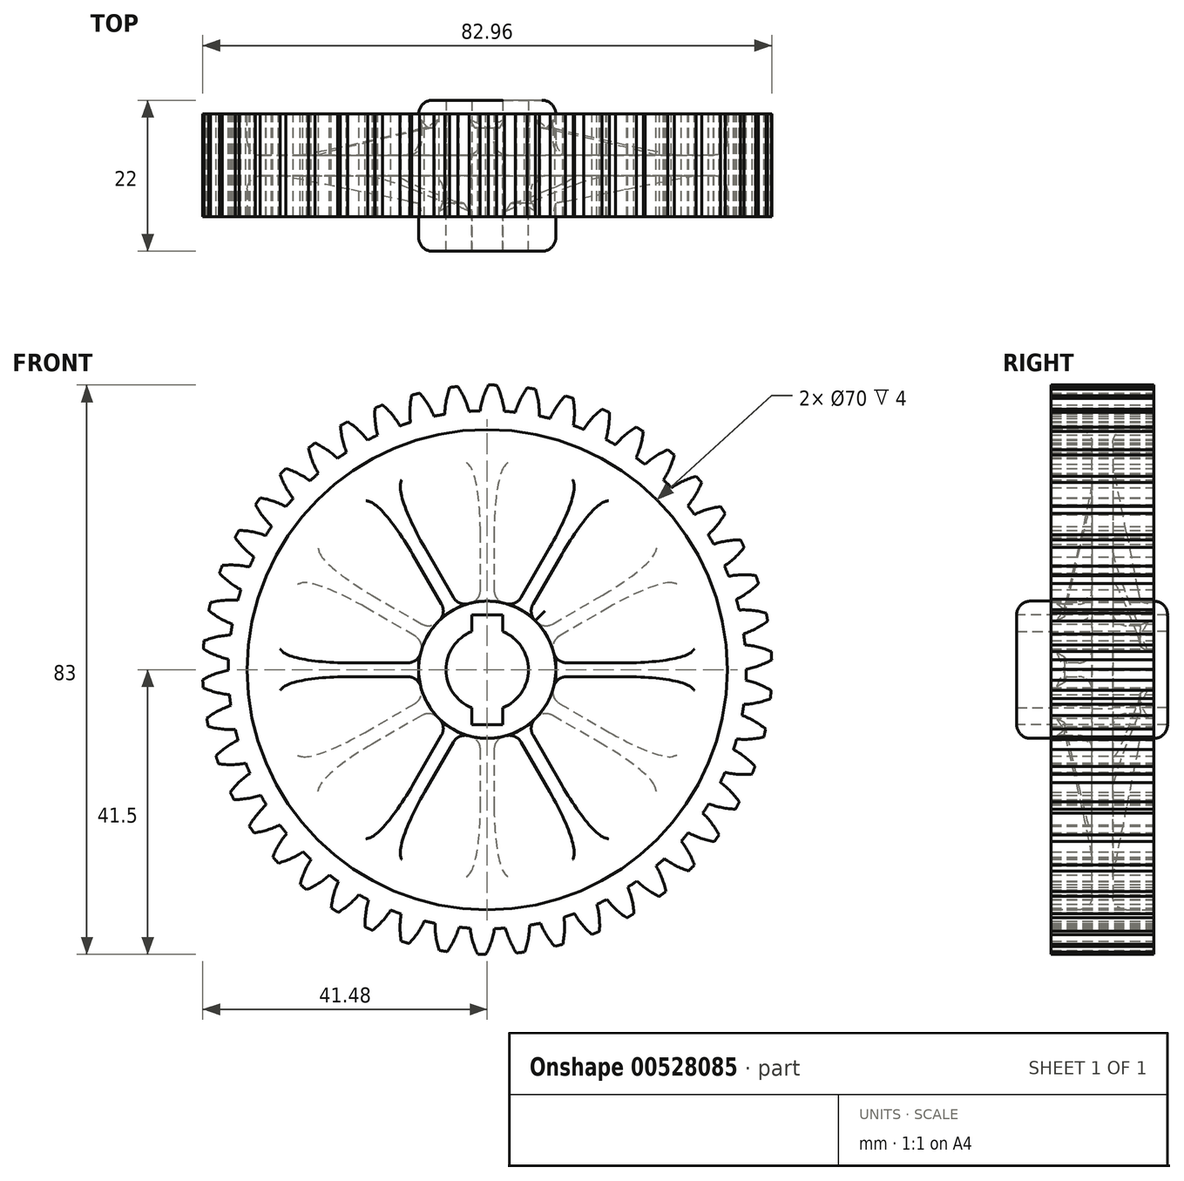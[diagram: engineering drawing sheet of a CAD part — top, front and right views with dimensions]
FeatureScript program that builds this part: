
annotation { "Feature Type Name" : "Feature", "Feature Type Description" : "" }
export const myFeature = defineFeature(function(context is Context, id is Id, definition is map)
    precondition{}
    {
        {
            var Q0;
            Q0=qCreatedBy(makeId("Front.planeOp"),FACE);
            var sketch = newSketch(context, id + "F0", { "sketchPlane" : qUnion([Q0])});
            skArc(sketch, "E0", {"start": v(1.4, 41.48) * mm, "mid": v(0.8, 41.5) * mm, "end": v(0.2, 41.5) * mm});
            skArc(sketch, "E1", {"start": v(4.12, 37.52) * mm, "mid": v(3.3, 37.6) * mm, "end": v(2.5, 37.67) * mm});
            skLineSegment(sketch, "E2", {"start": v(0, 0) * mm, "end": v(0.8, 41.5) * mm, "construction": true});
            skArc(sketch, "E3", {"start": v(0.2, 41.5) * mm, "mid": v(-0.59, 39.67) * mm, "end": v(-1.05, 37.74) * mm});
            skArc(sketch, "E4.MirrorCS", {"start": v(1.4, 41.48) * mm, "mid": v(2.1, 39.62) * mm, "end": v(2.5, 37.67) * mm});
            skArc(sketch, "E5.1.0", {"start": v(-4.27, 41.28) * mm, "mid": v(-3.31, 39.53) * mm, "end": v(-2.66, 37.66) * mm});
            skArc(sketch, "E5.1.1", {"start": v(-5.46, 41.14) * mm, "mid": v(-5.98, 39.22) * mm, "end": v(-6.18, 37.24) * mm});
            skArc(sketch, "E5.1.2", {"start": v(-4.27, 41.28) * mm, "mid": v(-4.86, 41.21) * mm, "end": v(-5.46, 41.14) * mm});
            skArc(sketch, "E5.1.3", {"start": v(-1.03, 37.74) * mm, "mid": v(-1.85, 37.7) * mm, "end": v(-2.66, 37.66) * mm});
            skArc(sketch, "E5.2.0", {"start": v(-9.85, 40.31) * mm, "mid": v(-8.67, 38.71) * mm, "end": v(-7.76, 36.94) * mm});
            skArc(sketch, "E5.2.1", {"start": v(-11.01, 40.01) * mm, "mid": v(-11.27, 38.04) * mm, "end": v(-11.2, 36.05) * mm});
            skArc(sketch, "E5.2.2", {"start": v(-9.85, 40.31) * mm, "mid": v(-10.43, 40.17) * mm, "end": v(-11.01, 40.01) * mm});
            skArc(sketch, "E5.2.3", {"start": v(-6.16, 37.24) * mm, "mid": v(-6.96, 37.1) * mm, "end": v(-7.76, 36.94) * mm});
            skArc(sketch, "E5.3.0", {"start": v(-15.25, 38.6) * mm, "mid": v(-13.86, 37.17) * mm, "end": v(-12.72, 35.54) * mm});
            skArc(sketch, "E5.3.1", {"start": v(-16.36, 38.14) * mm, "mid": v(-16.34, 36.15) * mm, "end": v(-16, 34.2) * mm});
            skArc(sketch, "E5.3.2", {"start": v(-15.25, 38.6) * mm, "mid": v(-15.8, 38.37) * mm, "end": v(-16.36, 38.14) * mm});
            skArc(sketch, "E5.3.3", {"start": v(-11.17, 36.06) * mm, "mid": v(-11.95, 35.8) * mm, "end": v(-12.72, 35.54) * mm});
            skArc(sketch, "E5.4.0", {"start": v(-20.36, 36.16) * mm, "mid": v(-18.8, 34.94) * mm, "end": v(-17.44, 33.48) * mm});
            skArc(sketch, "E5.4.1", {"start": v(-21.4, 35.56) * mm, "mid": v(-21.11, 33.59) * mm, "end": v(-20.5, 31.7) * mm});
            skArc(sketch, "E5.4.2", {"start": v(-20.36, 36.16) * mm, "mid": v(-20.88, 35.86) * mm, "end": v(-21.4, 35.56) * mm});
            skArc(sketch, "E5.4.3", {"start": v(-15.98, 34.2) * mm, "mid": v(-16.72, 33.85) * mm, "end": v(-17.44, 33.48) * mm});
            skArc(sketch, "E5.5.0", {"start": v(-25.1, 33.05) * mm, "mid": v(-23.37, 32.06) * mm, "end": v(-21.84, 30.8) * mm});
            skArc(sketch, "E5.5.1", {"start": v(-26.04, 32.31) * mm, "mid": v(-25.49, 30.4) * mm, "end": v(-24.63, 28.6) * mm});
            skArc(sketch, "E5.5.2", {"start": v(-25.1, 33.05) * mm, "mid": v(-25.57, 32.69) * mm, "end": v(-26.04, 32.31) * mm});
            skArc(sketch, "E5.5.3", {"start": v(-20.49, 31.7) * mm, "mid": v(-21.17, 31.26) * mm, "end": v(-21.84, 30.8) * mm});
            skArc(sketch, "E5.6.0", {"start": v(-29.36, 29.33) * mm, "mid": v(-27.52, 28.58) * mm, "end": v(-25.83, 27.53) * mm});
            skArc(sketch, "E5.6.1", {"start": v(-30.2, 28.47) * mm, "mid": v(-29.4, 26.65) * mm, "end": v(-28.3, 24.99) * mm});
            skArc(sketch, "E5.6.2", {"start": v(-29.36, 29.33) * mm, "mid": v(-29.78, 28.9) * mm, "end": v(-30.2, 28.47) * mm});
            skArc(sketch, "E5.6.3", {"start": v(-24.61, 28.62) * mm, "mid": v(-25.23, 28.08) * mm, "end": v(-25.83, 27.53) * mm});
            skArc(sketch, "E5.7.0", {"start": v(-33.08, 25.06) * mm, "mid": v(-31.16, 24.56) * mm, "end": v(-29.34, 23.76) * mm});
            skArc(sketch, "E5.7.1", {"start": v(-33.8, 24.09) * mm, "mid": v(-32.75, 22.4) * mm, "end": v(-31.44, 20.9) * mm});
            skArc(sketch, "E5.7.2", {"start": v(-33.08, 25.06) * mm, "mid": v(-33.44, 24.58) * mm, "end": v(-33.8, 24.09) * mm});
            skArc(sketch, "E5.7.3", {"start": v(-28.28, 25) * mm, "mid": v(-28.82, 24.39) * mm, "end": v(-29.34, 23.76) * mm});
            skArc(sketch, "E5.8.0", {"start": v(-36.19, 20.32) * mm, "mid": v(-34.2, 20.1) * mm, "end": v(-32.3, 19.54) * mm});
            skArc(sketch, "E5.8.1", {"start": v(-36.76, 19.26) * mm, "mid": v(-35.5, 17.73) * mm, "end": v(-33.99, 16.43) * mm});
            skArc(sketch, "E5.8.2", {"start": v(-36.19, 20.32) * mm, "mid": v(-36.48, 19.8) * mm, "end": v(-36.76, 19.26) * mm});
            skArc(sketch, "E5.8.3", {"start": v(-31.42, 20.92) * mm, "mid": v(-31.87, 20.24) * mm, "end": v(-32.3, 19.54) * mm});
            skArc(sketch, "E5.9.0", {"start": v(-38.62, 15.2) * mm, "mid": v(-36.63, 15.25) * mm, "end": v(-34.66, 14.96) * mm});
            skArc(sketch, "E5.9.1", {"start": v(-39.04, 14.08) * mm, "mid": v(-37.57, 12.73) * mm, "end": v(-35.9, 11.65) * mm});
            skArc(sketch, "E5.9.2", {"start": v(-38.62, 15.2) * mm, "mid": v(-38.83, 14.64) * mm, "end": v(-39.04, 14.08) * mm});
            skArc(sketch, "E5.9.3", {"start": v(-33.98, 16.45) * mm, "mid": v(-34.33, 15.7) * mm, "end": v(-34.66, 14.96) * mm});
            skArc(sketch, "E5.10.0", {"start": v(-40.33, 9.8) * mm, "mid": v(-38.36, 10.12) * mm, "end": v(-36.37, 10.1) * mm});
            skArc(sketch, "E5.10.1", {"start": v(-40.6, 8.63) * mm, "mid": v(-38.96, 7.5) * mm, "end": v(-37.16, 6.65) * mm});
            skArc(sketch, "E5.10.2", {"start": v(-40.33, 9.8) * mm, "mid": v(-40.46, 9.22) * mm, "end": v(-40.6, 8.63) * mm});
            skArc(sketch, "E5.10.3", {"start": v(-35.9, 11.67) * mm, "mid": v(-36.15, 10.89) * mm, "end": v(-36.37, 10.1) * mm});
            skArc(sketch, "E5.11.0", {"start": v(-41.28, 4.22) * mm, "mid": v(-39.38, 4.8) * mm, "end": v(-37.4, 5.06) * mm});
            skArc(sketch, "E5.11.1", {"start": v(-41.39, 3.02) * mm, "mid": v(-39.62, 2.12) * mm, "end": v(-37.72, 1.53) * mm});
            skArc(sketch, "E5.11.2", {"start": v(-41.28, 4.22) * mm, "mid": v(-41.34, 3.62) * mm, "end": v(-41.39, 3.02) * mm});
            skArc(sketch, "E5.11.3", {"start": v(-37.16, 6.67) * mm, "mid": v(-37.3, 5.86) * mm, "end": v(-37.4, 5.06) * mm});
            skArc(sketch, "E5.12.0", {"start": v(-41.48, -1.44) * mm, "mid": v(-39.67, -0.6) * mm, "end": v(-37.75, -0.08) * mm});
            skArc(sketch, "E5.12.1", {"start": v(-41.42, -2.64) * mm, "mid": v(-39.54, -3.3) * mm, "end": v(-37.58, -3.62) * mm});
            skArc(sketch, "E5.12.2", {"start": v(-41.48, -1.44) * mm, "mid": v(-41.45, -2.04) * mm, "end": v(-41.42, -2.64) * mm});
            skArc(sketch, "E5.12.3", {"start": v(-37.72, 1.55) * mm, "mid": v(-37.74, 0.73) * mm, "end": v(-37.75, -0.08) * mm});
            skArc(sketch, "E5.13.0", {"start": v(-40.9, -7.07) * mm, "mid": v(-39.22, -6) * mm, "end": v(-37.39, -5.22) * mm});
            skArc(sketch, "E5.13.1", {"start": v(-40.67, -8.26) * mm, "mid": v(-38.72, -8.64) * mm, "end": v(-36.73, -8.7) * mm});
            skArc(sketch, "E5.13.2", {"start": v(-40.9, -7.07) * mm, "mid": v(-40.79, -7.67) * mm, "end": v(-40.67, -8.26) * mm});
            skArc(sketch, "E5.13.3", {"start": v(-37.58, -3.6) * mm, "mid": v(-37.5, -4.42) * mm, "end": v(-37.39, -5.22) * mm});
            skArc(sketch, "E5.14.0", {"start": v(-39.55, -12.58) * mm, "mid": v(-38.03, -11.29) * mm, "end": v(-36.33, -10.27) * mm});
            skArc(sketch, "E5.14.1", {"start": v(-39.17, -13.72) * mm, "mid": v(-37.18, -13.84) * mm, "end": v(-35.2, -13.63) * mm});
            skArc(sketch, "E5.14.2", {"start": v(-39.55, -12.58) * mm, "mid": v(-39.36, -13.15) * mm, "end": v(-39.17, -13.72) * mm});
            skArc(sketch, "E5.14.3", {"start": v(-36.74, -8.69) * mm, "mid": v(-36.54, -9.48) * mm, "end": v(-36.33, -10.27) * mm});
            skArc(sketch, "E5.15.0", {"start": v(-37.47, -17.84) * mm, "mid": v(-36.14, -16.36) * mm, "end": v(-34.6, -15.12) * mm});
            skArc(sketch, "E5.15.1", {"start": v(-36.93, -18.92) * mm, "mid": v(-34.95, -18.77) * mm, "end": v(-33.02, -18.3) * mm});
            skArc(sketch, "E5.15.2", {"start": v(-37.47, -17.84) * mm, "mid": v(-37.2, -18.39) * mm, "end": v(-36.93, -18.92) * mm});
            skArc(sketch, "E5.15.3", {"start": v(-35.21, -13.6) * mm, "mid": v(-34.9, -14.37) * mm, "end": v(-34.6, -15.12) * mm});
            skArc(sketch, "E5.16.0", {"start": v(-34.69, -22.78) * mm, "mid": v(-33.58, -21.13) * mm, "end": v(-32.21, -19.69) * mm});
            skArc(sketch, "E5.16.1", {"start": v(-34.01, -23.78) * mm, "mid": v(-32.07, -23.35) * mm, "end": v(-30.22, -22.62) * mm});
            skArc(sketch, "E5.16.2", {"start": v(-34.69, -22.78) * mm, "mid": v(-34.36, -23.28) * mm, "end": v(-34.01, -23.78) * mm});
            skArc(sketch, "E5.16.3", {"start": v(-33.03, -18.28) * mm, "mid": v(-32.63, -18.99) * mm, "end": v(-32.21, -19.69) * mm});
            skArc(sketch, "E5.17.0", {"start": v(-31.26, -27.3) * mm, "mid": v(-30.39, -25.5) * mm, "end": v(-29.23, -23.89) * mm});
            skArc(sketch, "E5.17.1", {"start": v(-30.46, -28.19) * mm, "mid": v(-28.6, -27.5) * mm, "end": v(-26.86, -26.52) * mm});
            skArc(sketch, "E5.17.2", {"start": v(-31.26, -27.3) * mm, "mid": v(-30.87, -27.74) * mm, "end": v(-30.46, -28.19) * mm});
            skArc(sketch, "E5.17.3", {"start": v(-30.23, -22.6) * mm, "mid": v(-29.74, -23.25) * mm, "end": v(-29.23, -23.89) * mm});
            skArc(sketch, "E5.18.0", {"start": v(-27.26, -31.3) * mm, "mid": v(-26.63, -29.4) * mm, "end": v(-25.7, -27.65) * mm});
            skArc(sketch, "E5.18.1", {"start": v(-26.34, -32.07) * mm, "mid": v(-24.58, -31.14) * mm, "end": v(-23, -29.94) * mm});
            skArc(sketch, "E5.18.2", {"start": v(-27.26, -31.3) * mm, "mid": v(-26.8, -31.69) * mm, "end": v(-26.34, -32.07) * mm});
            skArc(sketch, "E5.18.3", {"start": v(-26.87, -26.51) * mm, "mid": v(-26.3, -27.08) * mm, "end": v(-25.7, -27.65) * mm});
            skArc(sketch, "E5.19.0", {"start": v(-22.74, -34.71) * mm, "mid": v(-22.38, -32.76) * mm, "end": v(-21.7, -30.89) * mm});
            skArc(sketch, "E5.19.1", {"start": v(-21.73, -35.36) * mm, "mid": v(-20.11, -34.2) * mm, "end": v(-18.7, -32.79) * mm});
            skArc(sketch, "E5.19.2", {"start": v(-22.74, -34.71) * mm, "mid": v(-22.24, -35.04) * mm, "end": v(-21.73, -35.36) * mm});
            skArc(sketch, "E5.19.3", {"start": v(-23.01, -29.92) * mm, "mid": v(-22.36, -30.41) * mm, "end": v(-21.7, -30.89) * mm});
            skArc(sketch, "E5.20.0", {"start": v(-17.8, -37.49) * mm, "mid": v(-17.7, -35.5) * mm, "end": v(-17.3, -33.56) * mm});
            skArc(sketch, "E5.20.1", {"start": v(-16.7, -37.99) * mm, "mid": v(-15.27, -36.62) * mm, "end": v(-14.07, -35.03) * mm});
            skArc(sketch, "E5.20.2", {"start": v(-17.8, -37.49) * mm, "mid": v(-17.26, -37.74) * mm, "end": v(-16.7, -37.99) * mm});
            skArc(sketch, "E5.20.3", {"start": v(-18.73, -32.78) * mm, "mid": v(-18.01, -33.18) * mm, "end": v(-17.3, -33.56) * mm});
            skArc(sketch, "E5.21.0", {"start": v(-12.53, -39.56) * mm, "mid": v(-12.71, -37.58) * mm, "end": v(-12.56, -35.6) * mm});
            skArc(sketch, "E5.21.1", {"start": v(-11.38, -39.9) * mm, "mid": v(-10.14, -38.36) * mm, "end": v(-9.17, -36.62) * mm});
            skArc(sketch, "E5.21.2", {"start": v(-12.53, -39.56) * mm, "mid": v(-11.96, -39.74) * mm, "end": v(-11.38, -39.9) * mm});
            skArc(sketch, "E5.21.3", {"start": v(-14.09, -35.02) * mm, "mid": v(-13.33, -35.32) * mm, "end": v(-12.56, -35.6) * mm});
            skArc(sketch, "E5.22.0", {"start": v(-7.03, -40.9) * mm, "mid": v(-7.47, -38.96) * mm, "end": v(-7.6, -36.98) * mm});
            skArc(sketch, "E5.22.1", {"start": v(-5.84, -41.09) * mm, "mid": v(-4.82, -39.38) * mm, "end": v(-4.1, -37.53) * mm});
            skArc(sketch, "E5.22.2", {"start": v(-7.03, -40.9) * mm, "mid": v(-6.44, -41) * mm, "end": v(-5.84, -41.09) * mm});
            skArc(sketch, "E5.22.3", {"start": v(-9.19, -36.61) * mm, "mid": v(-8.4, -36.8) * mm, "end": v(-7.6, -36.98) * mm});
            skArc(sketch, "E5.23.0", {"start": v(-1.4, -41.48) * mm, "mid": v(-2.1, -39.62) * mm, "end": v(-2.5, -37.67) * mm});
            skArc(sketch, "E5.23.1", {"start": v(-0.2, -41.5) * mm, "mid": v(0.59, -39.67) * mm, "end": v(1.05, -37.74) * mm});
            skArc(sketch, "E5.23.2", {"start": v(-1.4, -41.48) * mm, "mid": v(-0.8, -41.5) * mm, "end": v(-0.2, -41.5) * mm});
            skArc(sketch, "E5.23.3", {"start": v(-4.12, -37.52) * mm, "mid": v(-3.3, -37.6) * mm, "end": v(-2.5, -37.67) * mm});
            skArc(sketch, "E5.24.0", {"start": v(4.27, -41.28) * mm, "mid": v(3.31, -39.53) * mm, "end": v(2.66, -37.66) * mm});
            skArc(sketch, "E5.24.1", {"start": v(5.46, -41.14) * mm, "mid": v(5.98, -39.22) * mm, "end": v(6.18, -37.24) * mm});
            skArc(sketch, "E5.24.2", {"start": v(4.27, -41.28) * mm, "mid": v(4.86, -41.21) * mm, "end": v(5.46, -41.14) * mm});
            skArc(sketch, "E5.24.3", {"start": v(1.03, -37.74) * mm, "mid": v(1.85, -37.7) * mm, "end": v(2.66, -37.66) * mm});
            skArc(sketch, "E5.25.0", {"start": v(9.85, -40.31) * mm, "mid": v(8.67, -38.71) * mm, "end": v(7.76, -36.94) * mm});
            skArc(sketch, "E5.25.1", {"start": v(11.01, -40.01) * mm, "mid": v(11.27, -38.04) * mm, "end": v(11.2, -36.05) * mm});
            skArc(sketch, "E5.25.2", {"start": v(9.85, -40.31) * mm, "mid": v(10.43, -40.17) * mm, "end": v(11.01, -40.01) * mm});
            skArc(sketch, "E5.25.3", {"start": v(6.16, -37.24) * mm, "mid": v(6.96, -37.1) * mm, "end": v(7.76, -36.94) * mm});
            skArc(sketch, "E5.26.0", {"start": v(15.25, -38.6) * mm, "mid": v(13.86, -37.17) * mm, "end": v(12.72, -35.54) * mm});
            skArc(sketch, "E5.26.1", {"start": v(16.36, -38.14) * mm, "mid": v(16.34, -36.15) * mm, "end": v(16, -34.2) * mm});
            skArc(sketch, "E5.26.2", {"start": v(15.25, -38.6) * mm, "mid": v(15.8, -38.37) * mm, "end": v(16.36, -38.14) * mm});
            skArc(sketch, "E5.26.3", {"start": v(11.17, -36.06) * mm, "mid": v(11.95, -35.8) * mm, "end": v(12.72, -35.54) * mm});
            skArc(sketch, "E5.27.0", {"start": v(20.36, -36.16) * mm, "mid": v(18.8, -34.94) * mm, "end": v(17.44, -33.48) * mm});
            skArc(sketch, "E5.27.1", {"start": v(21.4, -35.56) * mm, "mid": v(21.11, -33.59) * mm, "end": v(20.5, -31.7) * mm});
            skArc(sketch, "E5.27.2", {"start": v(20.36, -36.16) * mm, "mid": v(20.88, -35.86) * mm, "end": v(21.4, -35.56) * mm});
            skArc(sketch, "E5.27.3", {"start": v(15.98, -34.2) * mm, "mid": v(16.72, -33.85) * mm, "end": v(17.44, -33.48) * mm});
            skArc(sketch, "E5.28.0", {"start": v(25.1, -33.05) * mm, "mid": v(23.37, -32.06) * mm, "end": v(21.84, -30.8) * mm});
            skArc(sketch, "E5.28.1", {"start": v(26.04, -32.31) * mm, "mid": v(25.49, -30.4) * mm, "end": v(24.63, -28.6) * mm});
            skArc(sketch, "E5.28.2", {"start": v(25.1, -33.05) * mm, "mid": v(25.57, -32.69) * mm, "end": v(26.04, -32.31) * mm});
            skArc(sketch, "E5.28.3", {"start": v(20.49, -31.7) * mm, "mid": v(21.17, -31.26) * mm, "end": v(21.84, -30.8) * mm});
            skArc(sketch, "E5.29.0", {"start": v(29.36, -29.33) * mm, "mid": v(27.52, -28.58) * mm, "end": v(25.83, -27.53) * mm});
            skArc(sketch, "E5.29.1", {"start": v(30.2, -28.47) * mm, "mid": v(29.4, -26.65) * mm, "end": v(28.3, -24.99) * mm});
            skArc(sketch, "E5.29.2", {"start": v(29.36, -29.33) * mm, "mid": v(29.78, -28.9) * mm, "end": v(30.2, -28.47) * mm});
            skArc(sketch, "E5.29.3", {"start": v(24.61, -28.62) * mm, "mid": v(25.23, -28.08) * mm, "end": v(25.83, -27.53) * mm});
            skArc(sketch, "E5.30.0", {"start": v(33.08, -25.06) * mm, "mid": v(31.16, -24.56) * mm, "end": v(29.34, -23.76) * mm});
            skArc(sketch, "E5.30.1", {"start": v(33.8, -24.09) * mm, "mid": v(32.75, -22.4) * mm, "end": v(31.44, -20.9) * mm});
            skArc(sketch, "E5.30.2", {"start": v(33.08, -25.06) * mm, "mid": v(33.44, -24.58) * mm, "end": v(33.8, -24.09) * mm});
            skArc(sketch, "E5.30.3", {"start": v(28.28, -25) * mm, "mid": v(28.82, -24.39) * mm, "end": v(29.34, -23.76) * mm});
            skArc(sketch, "E5.31.0", {"start": v(36.19, -20.32) * mm, "mid": v(34.2, -20.1) * mm, "end": v(32.3, -19.54) * mm});
            skArc(sketch, "E5.31.1", {"start": v(36.76, -19.26) * mm, "mid": v(35.5, -17.73) * mm, "end": v(33.99, -16.43) * mm});
            skArc(sketch, "E5.31.2", {"start": v(36.19, -20.32) * mm, "mid": v(36.48, -19.8) * mm, "end": v(36.76, -19.26) * mm});
            skArc(sketch, "E5.31.3", {"start": v(31.42, -20.92) * mm, "mid": v(31.87, -20.24) * mm, "end": v(32.3, -19.54) * mm});
            skArc(sketch, "E5.32.0", {"start": v(38.62, -15.2) * mm, "mid": v(36.63, -15.25) * mm, "end": v(34.66, -14.96) * mm});
            skArc(sketch, "E5.32.1", {"start": v(39.04, -14.08) * mm, "mid": v(37.57, -12.73) * mm, "end": v(35.9, -11.65) * mm});
            skArc(sketch, "E5.32.2", {"start": v(38.62, -15.2) * mm, "mid": v(38.83, -14.64) * mm, "end": v(39.04, -14.08) * mm});
            skArc(sketch, "E5.32.3", {"start": v(33.98, -16.45) * mm, "mid": v(34.33, -15.7) * mm, "end": v(34.66, -14.96) * mm});
            skArc(sketch, "E5.33.0", {"start": v(40.33, -9.8) * mm, "mid": v(38.36, -10.12) * mm, "end": v(36.37, -10.1) * mm});
            skArc(sketch, "E5.33.1", {"start": v(40.6, -8.63) * mm, "mid": v(38.96, -7.5) * mm, "end": v(37.16, -6.65) * mm});
            skArc(sketch, "E5.33.2", {"start": v(40.33, -9.8) * mm, "mid": v(40.46, -9.22) * mm, "end": v(40.6, -8.63) * mm});
            skArc(sketch, "E5.33.3", {"start": v(35.9, -11.67) * mm, "mid": v(36.15, -10.89) * mm, "end": v(36.37, -10.1) * mm});
            skArc(sketch, "E5.34.0", {"start": v(41.28, -4.22) * mm, "mid": v(39.38, -4.8) * mm, "end": v(37.4, -5.06) * mm});
            skArc(sketch, "E5.34.1", {"start": v(41.39, -3.02) * mm, "mid": v(39.62, -2.12) * mm, "end": v(37.72, -1.53) * mm});
            skArc(sketch, "E5.34.2", {"start": v(41.28, -4.22) * mm, "mid": v(41.34, -3.62) * mm, "end": v(41.39, -3.02) * mm});
            skArc(sketch, "E5.34.3", {"start": v(37.16, -6.67) * mm, "mid": v(37.3, -5.86) * mm, "end": v(37.4, -5.06) * mm});
            skArc(sketch, "E5.35.0", {"start": v(41.48, 1.44) * mm, "mid": v(39.67, 0.6) * mm, "end": v(37.75, 0.08) * mm});
            skArc(sketch, "E5.35.1", {"start": v(41.42, 2.64) * mm, "mid": v(39.54, 3.3) * mm, "end": v(37.58, 3.62) * mm});
            skArc(sketch, "E5.35.2", {"start": v(41.48, 1.44) * mm, "mid": v(41.45, 2.04) * mm, "end": v(41.42, 2.64) * mm});
            skArc(sketch, "E5.35.3", {"start": v(37.72, -1.55) * mm, "mid": v(37.74, -0.73) * mm, "end": v(37.75, 0.08) * mm});
            skArc(sketch, "E5.36.0", {"start": v(40.9, 7.07) * mm, "mid": v(39.22, 6) * mm, "end": v(37.39, 5.22) * mm});
            skArc(sketch, "E5.36.1", {"start": v(40.67, 8.26) * mm, "mid": v(38.72, 8.64) * mm, "end": v(36.73, 8.7) * mm});
            skArc(sketch, "E5.36.2", {"start": v(40.9, 7.07) * mm, "mid": v(40.79, 7.67) * mm, "end": v(40.67, 8.26) * mm});
            skArc(sketch, "E5.36.3", {"start": v(37.58, 3.6) * mm, "mid": v(37.5, 4.42) * mm, "end": v(37.39, 5.22) * mm});
            skArc(sketch, "E5.37.0", {"start": v(39.55, 12.58) * mm, "mid": v(38.03, 11.29) * mm, "end": v(36.33, 10.27) * mm});
            skArc(sketch, "E5.37.1", {"start": v(39.17, 13.72) * mm, "mid": v(37.18, 13.84) * mm, "end": v(35.2, 13.63) * mm});
            skArc(sketch, "E5.37.2", {"start": v(39.55, 12.58) * mm, "mid": v(39.36, 13.15) * mm, "end": v(39.17, 13.72) * mm});
            skArc(sketch, "E5.37.3", {"start": v(36.74, 8.69) * mm, "mid": v(36.54, 9.48) * mm, "end": v(36.33, 10.27) * mm});
            skArc(sketch, "E5.38.0", {"start": v(37.47, 17.84) * mm, "mid": v(36.14, 16.36) * mm, "end": v(34.6, 15.12) * mm});
            skArc(sketch, "E5.38.1", {"start": v(36.93, 18.92) * mm, "mid": v(34.95, 18.77) * mm, "end": v(33.02, 18.3) * mm});
            skArc(sketch, "E5.38.2", {"start": v(37.47, 17.84) * mm, "mid": v(37.2, 18.39) * mm, "end": v(36.93, 18.92) * mm});
            skArc(sketch, "E5.38.3", {"start": v(35.21, 13.6) * mm, "mid": v(34.9, 14.37) * mm, "end": v(34.6, 15.12) * mm});
            skArc(sketch, "E5.39.0", {"start": v(34.69, 22.78) * mm, "mid": v(33.58, 21.13) * mm, "end": v(32.21, 19.69) * mm});
            skArc(sketch, "E5.39.1", {"start": v(34.01, 23.78) * mm, "mid": v(32.07, 23.35) * mm, "end": v(30.22, 22.62) * mm});
            skArc(sketch, "E5.39.2", {"start": v(34.69, 22.78) * mm, "mid": v(34.36, 23.28) * mm, "end": v(34.01, 23.78) * mm});
            skArc(sketch, "E5.39.3", {"start": v(33.03, 18.28) * mm, "mid": v(32.63, 18.99) * mm, "end": v(32.21, 19.69) * mm});
            skArc(sketch, "E5.40.0", {"start": v(31.26, 27.3) * mm, "mid": v(30.39, 25.5) * mm, "end": v(29.23, 23.89) * mm});
            skArc(sketch, "E5.40.1", {"start": v(30.46, 28.19) * mm, "mid": v(28.6, 27.5) * mm, "end": v(26.86, 26.52) * mm});
            skArc(sketch, "E5.40.2", {"start": v(31.26, 27.3) * mm, "mid": v(30.87, 27.74) * mm, "end": v(30.46, 28.19) * mm});
            skArc(sketch, "E5.40.3", {"start": v(30.23, 22.6) * mm, "mid": v(29.74, 23.25) * mm, "end": v(29.23, 23.89) * mm});
            skArc(sketch, "E5.41.0", {"start": v(27.26, 31.3) * mm, "mid": v(26.63, 29.4) * mm, "end": v(25.7, 27.65) * mm});
            skArc(sketch, "E5.41.1", {"start": v(26.34, 32.07) * mm, "mid": v(24.58, 31.14) * mm, "end": v(23, 29.94) * mm});
            skArc(sketch, "E5.41.2", {"start": v(27.26, 31.3) * mm, "mid": v(26.8, 31.69) * mm, "end": v(26.34, 32.07) * mm});
            skArc(sketch, "E5.41.3", {"start": v(26.87, 26.51) * mm, "mid": v(26.3, 27.08) * mm, "end": v(25.7, 27.65) * mm});
            skArc(sketch, "E5.42.0", {"start": v(22.74, 34.71) * mm, "mid": v(22.38, 32.76) * mm, "end": v(21.7, 30.89) * mm});
            skArc(sketch, "E5.42.1", {"start": v(21.73, 35.36) * mm, "mid": v(20.11, 34.2) * mm, "end": v(18.7, 32.79) * mm});
            skArc(sketch, "E5.42.2", {"start": v(22.74, 34.71) * mm, "mid": v(22.24, 35.04) * mm, "end": v(21.73, 35.36) * mm});
            skArc(sketch, "E5.42.3", {"start": v(23.01, 29.92) * mm, "mid": v(22.36, 30.41) * mm, "end": v(21.7, 30.89) * mm});
            skArc(sketch, "E5.43.0", {"start": v(17.8, 37.49) * mm, "mid": v(17.7, 35.5) * mm, "end": v(17.3, 33.56) * mm});
            skArc(sketch, "E5.43.1", {"start": v(16.7, 37.99) * mm, "mid": v(15.27, 36.62) * mm, "end": v(14.07, 35.03) * mm});
            skArc(sketch, "E5.43.2", {"start": v(17.8, 37.49) * mm, "mid": v(17.26, 37.74) * mm, "end": v(16.7, 37.99) * mm});
            skArc(sketch, "E5.43.3", {"start": v(18.73, 32.78) * mm, "mid": v(18.01, 33.18) * mm, "end": v(17.3, 33.56) * mm});
            skArc(sketch, "E5.44.0", {"start": v(12.53, 39.56) * mm, "mid": v(12.71, 37.58) * mm, "end": v(12.56, 35.6) * mm});
            skArc(sketch, "E5.44.1", {"start": v(11.38, 39.9) * mm, "mid": v(10.14, 38.36) * mm, "end": v(9.17, 36.62) * mm});
            skArc(sketch, "E5.44.2", {"start": v(12.53, 39.56) * mm, "mid": v(11.96, 39.74) * mm, "end": v(11.38, 39.9) * mm});
            skArc(sketch, "E5.44.3", {"start": v(14.09, 35.02) * mm, "mid": v(13.33, 35.32) * mm, "end": v(12.56, 35.6) * mm});
            skArc(sketch, "E5.45.0", {"start": v(7.03, 40.9) * mm, "mid": v(7.47, 38.96) * mm, "end": v(7.6, 36.98) * mm});
            skArc(sketch, "E5.45.1", {"start": v(5.84, 41.09) * mm, "mid": v(4.82, 39.38) * mm, "end": v(4.1, 37.53) * mm});
            skArc(sketch, "E5.45.2", {"start": v(7.03, 40.9) * mm, "mid": v(6.44, 41) * mm, "end": v(5.84, 41.09) * mm});
            skArc(sketch, "E5.45.3", {"start": v(9.19, 36.61) * mm, "mid": v(8.4, 36.8) * mm, "end": v(7.6, 36.98) * mm});
            skCircle(sketch, "E6", {"center": v(0, 0) * mm, "radius": 6.1 * mm});
            skSolve(sketch);
        }
        {
            var Q0;
            Q0 = qSketchRegion(id + "F0", true);
            extrude(context, id + "F1", {"entities" : qUnion([Q0]), "depth" : 15 * mm, "offsetDistance" : 25 * mm});
        }
        {
            var Q0;
            Q0=makeQuery(id+"F1.opExtrude","CAP_FACE",FACE,{"disambiguationData":[OSD([sQuery(id+"F0.wireOp",EDGE,"E0"),sQuery(id+"F0.wireOp",EDGE,"E1"),sQuery(id+"F0.wireOp",EDGE,"E3"),sQuery(id+"F0.wireOp",EDGE,"E4.MirrorCS"),sQuery(id+"F0.wireOp",EDGE,"E5.1.0"),sQuery(id+"F0.wireOp",EDGE,"E5.1.1"),sQuery(id+"F0.wireOp",EDGE,"E5.1.2"),sQuery(id+"F0.wireOp",EDGE,"E5.1.3"),sQuery(id+"F0.wireOp",EDGE,"E5.2.0"),sQuery(id+"F0.wireOp",EDGE,"E5.2.1"),sQuery(id+"F0.wireOp",EDGE,"E5.2.2"),sQuery(id+"F0.wireOp",EDGE,"E5.2.3"),sQuery(id+"F0.wireOp",EDGE,"E5.3.0"),sQuery(id+"F0.wireOp",EDGE,"E5.3.1"),sQuery(id+"F0.wireOp",EDGE,"E5.3.2"),sQuery(id+"F0.wireOp",EDGE,"E5.3.3"),sQuery(id+"F0.wireOp",EDGE,"E5.4.0"),sQuery(id+"F0.wireOp",EDGE,"E5.4.1"),sQuery(id+"F0.wireOp",EDGE,"E5.4.2"),sQuery(id+"F0.wireOp",EDGE,"E5.4.3"),sQuery(id+"F0.wireOp",EDGE,"E5.5.0"),sQuery(id+"F0.wireOp",EDGE,"E5.5.1"),sQuery(id+"F0.wireOp",EDGE,"E5.5.2"),sQuery(id+"F0.wireOp",EDGE,"E5.5.3"),sQuery(id+"F0.wireOp",EDGE,"E5.6.0"),sQuery(id+"F0.wireOp",EDGE,"E5.6.1"),sQuery(id+"F0.wireOp",EDGE,"E5.6.2"),sQuery(id+"F0.wireOp",EDGE,"E5.6.3"),sQuery(id+"F0.wireOp",EDGE,"E5.7.0"),sQuery(id+"F0.wireOp",EDGE,"E5.7.1"),sQuery(id+"F0.wireOp",EDGE,"E5.7.2"),sQuery(id+"F0.wireOp",EDGE,"E5.7.3"),sQuery(id+"F0.wireOp",EDGE,"E5.8.0"),sQuery(id+"F0.wireOp",EDGE,"E5.8.1"),sQuery(id+"F0.wireOp",EDGE,"E5.8.2"),sQuery(id+"F0.wireOp",EDGE,"E5.8.3"),sQuery(id+"F0.wireOp",EDGE,"E5.9.0"),sQuery(id+"F0.wireOp",EDGE,"E5.9.1"),sQuery(id+"F0.wireOp",EDGE,"E5.9.2"),sQuery(id+"F0.wireOp",EDGE,"E5.9.3"),sQuery(id+"F0.wireOp",EDGE,"E5.10.0"),sQuery(id+"F0.wireOp",EDGE,"E5.10.1"),sQuery(id+"F0.wireOp",EDGE,"E5.10.2"),sQuery(id+"F0.wireOp",EDGE,"E5.10.3"),sQuery(id+"F0.wireOp",EDGE,"E5.11.0"),sQuery(id+"F0.wireOp",EDGE,"E5.11.1"),sQuery(id+"F0.wireOp",EDGE,"E5.11.2"),sQuery(id+"F0.wireOp",EDGE,"E5.11.3"),sQuery(id+"F0.wireOp",EDGE,"E5.12.0"),sQuery(id+"F0.wireOp",EDGE,"E5.12.1"),sQuery(id+"F0.wireOp",EDGE,"E5.12.2"),sQuery(id+"F0.wireOp",EDGE,"E5.12.3"),sQuery(id+"F0.wireOp",EDGE,"E5.13.0"),sQuery(id+"F0.wireOp",EDGE,"E5.13.1"),sQuery(id+"F0.wireOp",EDGE,"E5.13.2"),sQuery(id+"F0.wireOp",EDGE,"E5.13.3"),sQuery(id+"F0.wireOp",EDGE,"E5.14.0"),sQuery(id+"F0.wireOp",EDGE,"E5.14.1"),sQuery(id+"F0.wireOp",EDGE,"E5.14.2"),sQuery(id+"F0.wireOp",EDGE,"E5.14.3"),sQuery(id+"F0.wireOp",EDGE,"E5.15.0"),sQuery(id+"F0.wireOp",EDGE,"E5.15.1"),sQuery(id+"F0.wireOp",EDGE,"E5.15.2"),sQuery(id+"F0.wireOp",EDGE,"E5.15.3"),sQuery(id+"F0.wireOp",EDGE,"E5.16.0"),sQuery(id+"F0.wireOp",EDGE,"E5.16.1"),sQuery(id+"F0.wireOp",EDGE,"E5.16.2"),sQuery(id+"F0.wireOp",EDGE,"E5.16.3"),sQuery(id+"F0.wireOp",EDGE,"E5.17.0"),sQuery(id+"F0.wireOp",EDGE,"E5.17.1"),sQuery(id+"F0.wireOp",EDGE,"E5.17.2"),sQuery(id+"F0.wireOp",EDGE,"E5.17.3"),sQuery(id+"F0.wireOp",EDGE,"E5.18.0"),sQuery(id+"F0.wireOp",EDGE,"E5.18.1"),sQuery(id+"F0.wireOp",EDGE,"E5.18.2"),sQuery(id+"F0.wireOp",EDGE,"E5.18.3"),sQuery(id+"F0.wireOp",EDGE,"E5.19.0"),sQuery(id+"F0.wireOp",EDGE,"E5.19.1"),sQuery(id+"F0.wireOp",EDGE,"E5.19.2"),sQuery(id+"F0.wireOp",EDGE,"E5.19.3"),sQuery(id+"F0.wireOp",EDGE,"E5.20.0"),sQuery(id+"F0.wireOp",EDGE,"E5.20.1"),sQuery(id+"F0.wireOp",EDGE,"E5.20.2"),sQuery(id+"F0.wireOp",EDGE,"E5.20.3"),sQuery(id+"F0.wireOp",EDGE,"E5.21.0"),sQuery(id+"F0.wireOp",EDGE,"E5.21.1"),sQuery(id+"F0.wireOp",EDGE,"E5.21.2"),sQuery(id+"F0.wireOp",EDGE,"E5.21.3"),sQuery(id+"F0.wireOp",EDGE,"E5.22.0"),sQuery(id+"F0.wireOp",EDGE,"E5.22.1"),sQuery(id+"F0.wireOp",EDGE,"E5.22.2"),sQuery(id+"F0.wireOp",EDGE,"E5.22.3"),sQuery(id+"F0.wireOp",EDGE,"E5.23.0"),sQuery(id+"F0.wireOp",EDGE,"E5.23.1"),sQuery(id+"F0.wireOp",EDGE,"E5.23.2"),sQuery(id+"F0.wireOp",EDGE,"E5.23.3"),sQuery(id+"F0.wireOp",EDGE,"E5.24.0"),sQuery(id+"F0.wireOp",EDGE,"E5.24.1"),sQuery(id+"F0.wireOp",EDGE,"E5.24.2"),sQuery(id+"F0.wireOp",EDGE,"E5.24.3"),sQuery(id+"F0.wireOp",EDGE,"E5.25.0"),sQuery(id+"F0.wireOp",EDGE,"E5.25.1"),sQuery(id+"F0.wireOp",EDGE,"E5.25.2"),sQuery(id+"F0.wireOp",EDGE,"E5.25.3"),sQuery(id+"F0.wireOp",EDGE,"E5.26.0"),sQuery(id+"F0.wireOp",EDGE,"E5.26.1"),sQuery(id+"F0.wireOp",EDGE,"E5.26.2"),sQuery(id+"F0.wireOp",EDGE,"E5.26.3"),sQuery(id+"F0.wireOp",EDGE,"E5.27.0"),sQuery(id+"F0.wireOp",EDGE,"E5.27.1"),sQuery(id+"F0.wireOp",EDGE,"E5.27.2"),sQuery(id+"F0.wireOp",EDGE,"E5.27.3"),sQuery(id+"F0.wireOp",EDGE,"E5.28.0"),sQuery(id+"F0.wireOp",EDGE,"E5.28.1"),sQuery(id+"F0.wireOp",EDGE,"E5.28.2"),sQuery(id+"F0.wireOp",EDGE,"E5.28.3"),sQuery(id+"F0.wireOp",EDGE,"E5.29.0"),sQuery(id+"F0.wireOp",EDGE,"E5.29.1"),sQuery(id+"F0.wireOp",EDGE,"E5.29.2"),sQuery(id+"F0.wireOp",EDGE,"E5.29.3"),sQuery(id+"F0.wireOp",EDGE,"E5.30.0"),sQuery(id+"F0.wireOp",EDGE,"E5.30.1"),sQuery(id+"F0.wireOp",EDGE,"E5.30.2"),sQuery(id+"F0.wireOp",EDGE,"E5.30.3"),sQuery(id+"F0.wireOp",EDGE,"E5.31.0"),sQuery(id+"F0.wireOp",EDGE,"E5.31.1"),sQuery(id+"F0.wireOp",EDGE,"E5.31.2"),sQuery(id+"F0.wireOp",EDGE,"E5.31.3"),sQuery(id+"F0.wireOp",EDGE,"E5.32.0"),sQuery(id+"F0.wireOp",EDGE,"E5.32.1"),sQuery(id+"F0.wireOp",EDGE,"E5.32.2"),sQuery(id+"F0.wireOp",EDGE,"E5.32.3"),sQuery(id+"F0.wireOp",EDGE,"E5.33.0"),sQuery(id+"F0.wireOp",EDGE,"E5.33.1"),sQuery(id+"F0.wireOp",EDGE,"E5.33.2"),sQuery(id+"F0.wireOp",EDGE,"E5.33.3"),sQuery(id+"F0.wireOp",EDGE,"E5.34.0"),sQuery(id+"F0.wireOp",EDGE,"E5.34.1"),sQuery(id+"F0.wireOp",EDGE,"E5.34.2"),sQuery(id+"F0.wireOp",EDGE,"E5.34.3"),sQuery(id+"F0.wireOp",EDGE,"E5.35.0"),sQuery(id+"F0.wireOp",EDGE,"E5.35.1"),sQuery(id+"F0.wireOp",EDGE,"E5.35.2"),sQuery(id+"F0.wireOp",EDGE,"E5.35.3"),sQuery(id+"F0.wireOp",EDGE,"E5.36.0"),sQuery(id+"F0.wireOp",EDGE,"E5.36.1"),sQuery(id+"F0.wireOp",EDGE,"E5.36.2"),sQuery(id+"F0.wireOp",EDGE,"E5.36.3"),sQuery(id+"F0.wireOp",EDGE,"E5.37.0"),sQuery(id+"F0.wireOp",EDGE,"E5.37.1"),sQuery(id+"F0.wireOp",EDGE,"E5.37.2"),sQuery(id+"F0.wireOp",EDGE,"E5.37.3"),sQuery(id+"F0.wireOp",EDGE,"E5.38.0"),sQuery(id+"F0.wireOp",EDGE,"E5.38.1"),sQuery(id+"F0.wireOp",EDGE,"E5.38.2"),sQuery(id+"F0.wireOp",EDGE,"E5.38.3"),sQuery(id+"F0.wireOp",EDGE,"E5.39.0"),sQuery(id+"F0.wireOp",EDGE,"E5.39.1"),sQuery(id+"F0.wireOp",EDGE,"E5.39.2"),sQuery(id+"F0.wireOp",EDGE,"E5.39.3"),sQuery(id+"F0.wireOp",EDGE,"E5.40.0"),sQuery(id+"F0.wireOp",EDGE,"E5.40.1"),sQuery(id+"F0.wireOp",EDGE,"E5.40.2"),sQuery(id+"F0.wireOp",EDGE,"E5.40.3"),sQuery(id+"F0.wireOp",EDGE,"E5.41.0"),sQuery(id+"F0.wireOp",EDGE,"E5.41.1"),sQuery(id+"F0.wireOp",EDGE,"E5.41.2"),sQuery(id+"F0.wireOp",EDGE,"E5.41.3"),sQuery(id+"F0.wireOp",EDGE,"E5.42.0"),sQuery(id+"F0.wireOp",EDGE,"E5.42.1"),sQuery(id+"F0.wireOp",EDGE,"E5.42.2"),sQuery(id+"F0.wireOp",EDGE,"E5.42.3"),sQuery(id+"F0.wireOp",EDGE,"E5.43.0"),sQuery(id+"F0.wireOp",EDGE,"E5.43.1"),sQuery(id+"F0.wireOp",EDGE,"E5.43.2"),sQuery(id+"F0.wireOp",EDGE,"E5.43.3"),sQuery(id+"F0.wireOp",EDGE,"E5.44.0"),sQuery(id+"F0.wireOp",EDGE,"E5.44.1"),sQuery(id+"F0.wireOp",EDGE,"E5.44.2"),sQuery(id+"F0.wireOp",EDGE,"E5.44.3"),sQuery(id+"F0.wireOp",EDGE,"E5.45.0"),sQuery(id+"F0.wireOp",EDGE,"E5.45.1"),sQuery(id+"F0.wireOp",EDGE,"E5.45.2"),sQuery(id+"F0.wireOp",EDGE,"E5.45.3"),sQuery(id+"F0.wireOp",EDGE,"E6")])],"isStart":true});
            var sketch = newSketch(context, id + "F2", { "sketchPlane" : qUnion([Q0])});
            skCircle(sketch, "E7", {"center": v(0, 0) * mm, "radius": 35 * mm});
            skSolve(sketch);
        }
        {
            var Q0;
            Q0 = qSketchRegion(id + "F2", true);
            extrude(context, id + "F3", {"entities" : qUnion([Q0]), "operationType" : NewBodyOperationType.REMOVE, "oppositeDirection" : true, "depth" : 6 * mm, "offsetDistance" : 25 * mm});
        }
        {
            var Q0;
            Q0=makeQuery(id+"F1.opExtrude","CAP_FACE",FACE,{"disambiguationData":[OSD([sQuery(id+"F0.wireOp",EDGE,"E0"),sQuery(id+"F0.wireOp",EDGE,"E1"),sQuery(id+"F0.wireOp",EDGE,"E3"),sQuery(id+"F0.wireOp",EDGE,"E4.MirrorCS"),sQuery(id+"F0.wireOp",EDGE,"E5.1.0"),sQuery(id+"F0.wireOp",EDGE,"E5.1.1"),sQuery(id+"F0.wireOp",EDGE,"E5.1.2"),sQuery(id+"F0.wireOp",EDGE,"E5.1.3"),sQuery(id+"F0.wireOp",EDGE,"E5.2.0"),sQuery(id+"F0.wireOp",EDGE,"E5.2.1"),sQuery(id+"F0.wireOp",EDGE,"E5.2.2"),sQuery(id+"F0.wireOp",EDGE,"E5.2.3"),sQuery(id+"F0.wireOp",EDGE,"E5.3.0"),sQuery(id+"F0.wireOp",EDGE,"E5.3.1"),sQuery(id+"F0.wireOp",EDGE,"E5.3.2"),sQuery(id+"F0.wireOp",EDGE,"E5.3.3"),sQuery(id+"F0.wireOp",EDGE,"E5.4.0"),sQuery(id+"F0.wireOp",EDGE,"E5.4.1"),sQuery(id+"F0.wireOp",EDGE,"E5.4.2"),sQuery(id+"F0.wireOp",EDGE,"E5.4.3"),sQuery(id+"F0.wireOp",EDGE,"E5.5.0"),sQuery(id+"F0.wireOp",EDGE,"E5.5.1"),sQuery(id+"F0.wireOp",EDGE,"E5.5.2"),sQuery(id+"F0.wireOp",EDGE,"E5.5.3"),sQuery(id+"F0.wireOp",EDGE,"E5.6.0"),sQuery(id+"F0.wireOp",EDGE,"E5.6.1"),sQuery(id+"F0.wireOp",EDGE,"E5.6.2"),sQuery(id+"F0.wireOp",EDGE,"E5.6.3"),sQuery(id+"F0.wireOp",EDGE,"E5.7.0"),sQuery(id+"F0.wireOp",EDGE,"E5.7.1"),sQuery(id+"F0.wireOp",EDGE,"E5.7.2"),sQuery(id+"F0.wireOp",EDGE,"E5.7.3"),sQuery(id+"F0.wireOp",EDGE,"E5.8.0"),sQuery(id+"F0.wireOp",EDGE,"E5.8.1"),sQuery(id+"F0.wireOp",EDGE,"E5.8.2"),sQuery(id+"F0.wireOp",EDGE,"E5.8.3"),sQuery(id+"F0.wireOp",EDGE,"E5.9.0"),sQuery(id+"F0.wireOp",EDGE,"E5.9.1"),sQuery(id+"F0.wireOp",EDGE,"E5.9.2"),sQuery(id+"F0.wireOp",EDGE,"E5.9.3"),sQuery(id+"F0.wireOp",EDGE,"E5.10.0"),sQuery(id+"F0.wireOp",EDGE,"E5.10.1"),sQuery(id+"F0.wireOp",EDGE,"E5.10.2"),sQuery(id+"F0.wireOp",EDGE,"E5.10.3"),sQuery(id+"F0.wireOp",EDGE,"E5.11.0"),sQuery(id+"F0.wireOp",EDGE,"E5.11.1"),sQuery(id+"F0.wireOp",EDGE,"E5.11.2"),sQuery(id+"F0.wireOp",EDGE,"E5.11.3"),sQuery(id+"F0.wireOp",EDGE,"E5.12.0"),sQuery(id+"F0.wireOp",EDGE,"E5.12.1"),sQuery(id+"F0.wireOp",EDGE,"E5.12.2"),sQuery(id+"F0.wireOp",EDGE,"E5.12.3"),sQuery(id+"F0.wireOp",EDGE,"E5.13.0"),sQuery(id+"F0.wireOp",EDGE,"E5.13.1"),sQuery(id+"F0.wireOp",EDGE,"E5.13.2"),sQuery(id+"F0.wireOp",EDGE,"E5.13.3"),sQuery(id+"F0.wireOp",EDGE,"E5.14.0"),sQuery(id+"F0.wireOp",EDGE,"E5.14.1"),sQuery(id+"F0.wireOp",EDGE,"E5.14.2"),sQuery(id+"F0.wireOp",EDGE,"E5.14.3"),sQuery(id+"F0.wireOp",EDGE,"E5.15.0"),sQuery(id+"F0.wireOp",EDGE,"E5.15.1"),sQuery(id+"F0.wireOp",EDGE,"E5.15.2"),sQuery(id+"F0.wireOp",EDGE,"E5.15.3"),sQuery(id+"F0.wireOp",EDGE,"E5.16.0"),sQuery(id+"F0.wireOp",EDGE,"E5.16.1"),sQuery(id+"F0.wireOp",EDGE,"E5.16.2"),sQuery(id+"F0.wireOp",EDGE,"E5.16.3"),sQuery(id+"F0.wireOp",EDGE,"E5.17.0"),sQuery(id+"F0.wireOp",EDGE,"E5.17.1"),sQuery(id+"F0.wireOp",EDGE,"E5.17.2"),sQuery(id+"F0.wireOp",EDGE,"E5.17.3"),sQuery(id+"F0.wireOp",EDGE,"E5.18.0"),sQuery(id+"F0.wireOp",EDGE,"E5.18.1"),sQuery(id+"F0.wireOp",EDGE,"E5.18.2"),sQuery(id+"F0.wireOp",EDGE,"E5.18.3"),sQuery(id+"F0.wireOp",EDGE,"E5.19.0"),sQuery(id+"F0.wireOp",EDGE,"E5.19.1"),sQuery(id+"F0.wireOp",EDGE,"E5.19.2"),sQuery(id+"F0.wireOp",EDGE,"E5.19.3"),sQuery(id+"F0.wireOp",EDGE,"E5.20.0"),sQuery(id+"F0.wireOp",EDGE,"E5.20.1"),sQuery(id+"F0.wireOp",EDGE,"E5.20.2"),sQuery(id+"F0.wireOp",EDGE,"E5.20.3"),sQuery(id+"F0.wireOp",EDGE,"E5.21.0"),sQuery(id+"F0.wireOp",EDGE,"E5.21.1"),sQuery(id+"F0.wireOp",EDGE,"E5.21.2"),sQuery(id+"F0.wireOp",EDGE,"E5.21.3"),sQuery(id+"F0.wireOp",EDGE,"E5.22.0"),sQuery(id+"F0.wireOp",EDGE,"E5.22.1"),sQuery(id+"F0.wireOp",EDGE,"E5.22.2"),sQuery(id+"F0.wireOp",EDGE,"E5.22.3"),sQuery(id+"F0.wireOp",EDGE,"E5.23.0"),sQuery(id+"F0.wireOp",EDGE,"E5.23.1"),sQuery(id+"F0.wireOp",EDGE,"E5.23.2"),sQuery(id+"F0.wireOp",EDGE,"E5.23.3"),sQuery(id+"F0.wireOp",EDGE,"E5.24.0"),sQuery(id+"F0.wireOp",EDGE,"E5.24.1"),sQuery(id+"F0.wireOp",EDGE,"E5.24.2"),sQuery(id+"F0.wireOp",EDGE,"E5.24.3"),sQuery(id+"F0.wireOp",EDGE,"E5.25.0"),sQuery(id+"F0.wireOp",EDGE,"E5.25.1"),sQuery(id+"F0.wireOp",EDGE,"E5.25.2"),sQuery(id+"F0.wireOp",EDGE,"E5.25.3"),sQuery(id+"F0.wireOp",EDGE,"E5.26.0"),sQuery(id+"F0.wireOp",EDGE,"E5.26.1"),sQuery(id+"F0.wireOp",EDGE,"E5.26.2"),sQuery(id+"F0.wireOp",EDGE,"E5.26.3"),sQuery(id+"F0.wireOp",EDGE,"E5.27.0"),sQuery(id+"F0.wireOp",EDGE,"E5.27.1"),sQuery(id+"F0.wireOp",EDGE,"E5.27.2"),sQuery(id+"F0.wireOp",EDGE,"E5.27.3"),sQuery(id+"F0.wireOp",EDGE,"E5.28.0"),sQuery(id+"F0.wireOp",EDGE,"E5.28.1"),sQuery(id+"F0.wireOp",EDGE,"E5.28.2"),sQuery(id+"F0.wireOp",EDGE,"E5.28.3"),sQuery(id+"F0.wireOp",EDGE,"E5.29.0"),sQuery(id+"F0.wireOp",EDGE,"E5.29.1"),sQuery(id+"F0.wireOp",EDGE,"E5.29.2"),sQuery(id+"F0.wireOp",EDGE,"E5.29.3"),sQuery(id+"F0.wireOp",EDGE,"E5.30.0"),sQuery(id+"F0.wireOp",EDGE,"E5.30.1"),sQuery(id+"F0.wireOp",EDGE,"E5.30.2"),sQuery(id+"F0.wireOp",EDGE,"E5.30.3"),sQuery(id+"F0.wireOp",EDGE,"E5.31.0"),sQuery(id+"F0.wireOp",EDGE,"E5.31.1"),sQuery(id+"F0.wireOp",EDGE,"E5.31.2"),sQuery(id+"F0.wireOp",EDGE,"E5.31.3"),sQuery(id+"F0.wireOp",EDGE,"E5.32.0"),sQuery(id+"F0.wireOp",EDGE,"E5.32.1"),sQuery(id+"F0.wireOp",EDGE,"E5.32.2"),sQuery(id+"F0.wireOp",EDGE,"E5.32.3"),sQuery(id+"F0.wireOp",EDGE,"E5.33.0"),sQuery(id+"F0.wireOp",EDGE,"E5.33.1"),sQuery(id+"F0.wireOp",EDGE,"E5.33.2"),sQuery(id+"F0.wireOp",EDGE,"E5.33.3"),sQuery(id+"F0.wireOp",EDGE,"E5.34.0"),sQuery(id+"F0.wireOp",EDGE,"E5.34.1"),sQuery(id+"F0.wireOp",EDGE,"E5.34.2"),sQuery(id+"F0.wireOp",EDGE,"E5.34.3"),sQuery(id+"F0.wireOp",EDGE,"E5.35.0"),sQuery(id+"F0.wireOp",EDGE,"E5.35.1"),sQuery(id+"F0.wireOp",EDGE,"E5.35.2"),sQuery(id+"F0.wireOp",EDGE,"E5.35.3"),sQuery(id+"F0.wireOp",EDGE,"E5.36.0"),sQuery(id+"F0.wireOp",EDGE,"E5.36.1"),sQuery(id+"F0.wireOp",EDGE,"E5.36.2"),sQuery(id+"F0.wireOp",EDGE,"E5.36.3"),sQuery(id+"F0.wireOp",EDGE,"E5.37.0"),sQuery(id+"F0.wireOp",EDGE,"E5.37.1"),sQuery(id+"F0.wireOp",EDGE,"E5.37.2"),sQuery(id+"F0.wireOp",EDGE,"E5.37.3"),sQuery(id+"F0.wireOp",EDGE,"E5.38.0"),sQuery(id+"F0.wireOp",EDGE,"E5.38.1"),sQuery(id+"F0.wireOp",EDGE,"E5.38.2"),sQuery(id+"F0.wireOp",EDGE,"E5.38.3"),sQuery(id+"F0.wireOp",EDGE,"E5.39.0"),sQuery(id+"F0.wireOp",EDGE,"E5.39.1"),sQuery(id+"F0.wireOp",EDGE,"E5.39.2"),sQuery(id+"F0.wireOp",EDGE,"E5.39.3"),sQuery(id+"F0.wireOp",EDGE,"E5.40.0"),sQuery(id+"F0.wireOp",EDGE,"E5.40.1"),sQuery(id+"F0.wireOp",EDGE,"E5.40.2"),sQuery(id+"F0.wireOp",EDGE,"E5.40.3"),sQuery(id+"F0.wireOp",EDGE,"E5.41.0"),sQuery(id+"F0.wireOp",EDGE,"E5.41.1"),sQuery(id+"F0.wireOp",EDGE,"E5.41.2"),sQuery(id+"F0.wireOp",EDGE,"E5.41.3"),sQuery(id+"F0.wireOp",EDGE,"E5.42.0"),sQuery(id+"F0.wireOp",EDGE,"E5.42.1"),sQuery(id+"F0.wireOp",EDGE,"E5.42.2"),sQuery(id+"F0.wireOp",EDGE,"E5.42.3"),sQuery(id+"F0.wireOp",EDGE,"E5.43.0"),sQuery(id+"F0.wireOp",EDGE,"E5.43.1"),sQuery(id+"F0.wireOp",EDGE,"E5.43.2"),sQuery(id+"F0.wireOp",EDGE,"E5.43.3"),sQuery(id+"F0.wireOp",EDGE,"E5.44.0"),sQuery(id+"F0.wireOp",EDGE,"E5.44.1"),sQuery(id+"F0.wireOp",EDGE,"E5.44.2"),sQuery(id+"F0.wireOp",EDGE,"E5.44.3"),sQuery(id+"F0.wireOp",EDGE,"E5.45.0"),sQuery(id+"F0.wireOp",EDGE,"E5.45.1"),sQuery(id+"F0.wireOp",EDGE,"E5.45.2"),sQuery(id+"F0.wireOp",EDGE,"E5.45.3"),sQuery(id+"F0.wireOp",EDGE,"E6")])],"isStart":false});
            var sketch = newSketch(context, id + "F4", { "sketchPlane" : qUnion([Q0])});
            skCircle(sketch, "E8", {"center": v(0, 0) * mm, "radius": 35 * mm});
            skSolve(sketch);
        }
        {
            var Q0;
            Q0 = qSketchRegion(id + "F4", true);
            extrude(context, id + "F5", {"entities" : qUnion([Q0]), "operationType" : NewBodyOperationType.REMOVE, "oppositeDirection" : true, "depth" : 6 * mm, "offsetDistance" : 25 * mm});
        }
        {
            var Q0;
            Q0=makeQuery(id+"F3.boolean.opBoolean","COPY",FACE,{"derivedFrom":makeQuery(id+"F3.opExtrude","CAP_FACE",FACE,{"disambiguationData":[OSD([sQuery(id+"F2.wireOp",EDGE,"E7")])],"isStart":false})});
            var sketch = newSketch(context, id + "F6", { "sketchPlane" : qUnion([Q0])});
            skCircle(sketch, "E9", {"center": v(0, 0) * mm, "radius": 10 * mm});
            skCircle(sketch, "E10", {"center": v(0, 0) * mm, "radius": 6 * mm});
            skSolve(sketch);
        }
        {
            var Q0;
            Q0 = qSketchRegion(id + "F6", true);
            extrude(context, id + "F7", {"entities" : qUnion([Q0]), "operationType" : NewBodyOperationType.ADD, "depth" : 8 * mm, "offsetDistance" : 25 * mm});
        }
        {
            var Q0;
            Q0=makeQuery(id+"F5.boolean.opBoolean","COPY",FACE,{"derivedFrom":makeQuery(id+"F5.opExtrude","CAP_FACE",FACE,{"disambiguationData":[OSD([sQuery(id+"F4.wireOp",EDGE,"E8")])],"isStart":false})});
            var sketch = newSketch(context, id + "F8", { "sketchPlane" : qUnion([Q0])});
            skCircle(sketch, "E11", {"center": v(0, 0) * mm, "radius": 10 * mm});
            skCircle(sketch, "E12", {"center": v(0, 0) * mm, "radius": 6 * mm});
            skSolve(sketch);
        }
        {
            var Q0;
            Q0 = qSketchRegion(id + "F8", true);
            extrude(context, id + "F9", {"entities" : qUnion([Q0]), "operationType" : NewBodyOperationType.ADD, "depth" : 11 * mm, "offsetDistance" : 25 * mm});
        }
        {
            var Q0;
            Q0=makeQuery(id+"F5.boolean.opBoolean","COPY",FACE,{"derivedFrom":makeQuery(id+"F5.opExtrude","CAP_FACE",FACE,{"disambiguationData":[OSD([sQuery(id+"F4.wireOp",EDGE,"E8")])],"isStart":false})});
            var sketch = newSketch(context, id + "F10", { "sketchPlane" : qUnion([Q0])});
            skLineSegment(sketch, "E13", {"start": v(0, 0) * mm, "end": v(3.97, 0) * mm, "construction": true});
            skLineSegment(sketch, "E14.bottom", {"start": v(30, 1) * mm, "end": v(9, 1) * mm});
            skLineSegment(sketch, "E14.top", {"start": v(30, -1) * mm, "end": v(9, -1) * mm});
            skLineSegment(sketch, "E14.left", {"start": v(30, 1) * mm, "end": v(30, -1) * mm});
            skLineSegment(sketch, "E14.right", {"start": v(9, 1) * mm, "end": v(9, -1) * mm});
            skLineSegment(sketch, "E15.1.0", {"start": v(15.87, 25.48) * mm, "end": v(5.37, 7.3) * mm});
            skLineSegment(sketch, "E15.1.1", {"start": v(14.13, 26.48) * mm, "end": v(3.63, 8.3) * mm});
            skLineSegment(sketch, "E15.1.2", {"start": v(0, 0) * mm, "end": v(1.98, 3.44) * mm, "construction": true});
            skLineSegment(sketch, "E15.1.3", {"start": v(3.63, 8.3) * mm, "end": v(5.37, 7.3) * mm});
            skLineSegment(sketch, "E15.1.4", {"start": v(14.13, 26.48) * mm, "end": v(15.87, 25.48) * mm});
            skLineSegment(sketch, "E15.2.0", {"start": v(-14.13, 26.48) * mm, "end": v(-3.63, 8.3) * mm});
            skLineSegment(sketch, "E15.2.1", {"start": v(-15.87, 25.48) * mm, "end": v(-5.37, 7.3) * mm});
            skLineSegment(sketch, "E15.2.2", {"start": v(0, 0) * mm, "end": v(-1.98, 3.44) * mm, "construction": true});
            skLineSegment(sketch, "E15.2.3", {"start": v(-5.37, 7.3) * mm, "end": v(-3.63, 8.3) * mm});
            skLineSegment(sketch, "E15.2.4", {"start": v(-15.87, 25.48) * mm, "end": v(-14.13, 26.48) * mm});
            skLineSegment(sketch, "E15.3.0", {"start": v(-30, 1) * mm, "end": v(-9, 1) * mm});
            skLineSegment(sketch, "E15.3.1", {"start": v(-30, -1) * mm, "end": v(-9, -1) * mm});
            skLineSegment(sketch, "E15.3.2", {"start": v(0, 0) * mm, "end": v(-3.97, 0) * mm, "construction": true});
            skLineSegment(sketch, "E15.3.3", {"start": v(-9, -1) * mm, "end": v(-9, 1) * mm});
            skLineSegment(sketch, "E15.3.4", {"start": v(-30, -1) * mm, "end": v(-30, 1) * mm});
            skLineSegment(sketch, "E15.4.0", {"start": v(-15.87, -25.48) * mm, "end": v(-5.37, -7.3) * mm});
            skLineSegment(sketch, "E15.4.1", {"start": v(-14.13, -26.48) * mm, "end": v(-3.63, -8.3) * mm});
            skLineSegment(sketch, "E15.4.2", {"start": v(0, 0) * mm, "end": v(-1.98, -3.44) * mm, "construction": true});
            skLineSegment(sketch, "E15.4.3", {"start": v(-3.63, -8.3) * mm, "end": v(-5.37, -7.3) * mm});
            skLineSegment(sketch, "E15.4.4", {"start": v(-14.13, -26.48) * mm, "end": v(-15.87, -25.48) * mm});
            skLineSegment(sketch, "E15.5.0", {"start": v(14.13, -26.48) * mm, "end": v(3.63, -8.3) * mm});
            skLineSegment(sketch, "E15.5.1", {"start": v(15.87, -25.48) * mm, "end": v(5.37, -7.3) * mm});
            skLineSegment(sketch, "E15.5.2", {"start": v(0, 0) * mm, "end": v(1.98, -3.44) * mm, "construction": true});
            skLineSegment(sketch, "E15.5.3", {"start": v(5.37, -7.3) * mm, "end": v(3.63, -8.3) * mm});
            skLineSegment(sketch, "E15.5.4", {"start": v(15.87, -25.48) * mm, "end": v(14.13, -26.48) * mm});
            skPoint(sketch, "E15.center", {"position": v(0, 0) * mm});
            skSolve(sketch);
        }
        {
            var Q0;
            Q0 = qSketchRegion(id + "F10", true);
            extrude(context, id + "F11", {"entities" : qUnion([Q0]), "operationType" : NewBodyOperationType.ADD, "depth" : 4 * mm, "offsetDistance" : 25 * mm});
        }
        {
            var Q0;
            Q0=makeQuery(id+"F11.opExtrude","CAP_EDGE",EDGE,{"disambiguationData":[OSD([sQuery(id+"F10.wireOp",EDGE,"E14.left")])],"isStart":false});
            var Q1;
            Q1=makeQuery(id+"F11.opExtrude","CAP_EDGE",EDGE,{"disambiguationData":[OSD([sQuery(id+"F10.wireOp",EDGE,"E15.5.4")])],"isStart":false});
            var Q2;
            Q2=makeQuery(id+"F11.opExtrude","CAP_EDGE",EDGE,{"disambiguationData":[OSD([sQuery(id+"F10.wireOp",EDGE,"E15.4.4")])],"isStart":false});
            var Q3;
            Q3=makeQuery(id+"F11.opExtrude","CAP_EDGE",EDGE,{"disambiguationData":[OSD([sQuery(id+"F10.wireOp",EDGE,"E15.3.4")])],"isStart":false});
            var Q4;
            Q4=makeQuery(id+"F11.opExtrude","CAP_EDGE",EDGE,{"disambiguationData":[OSD([sQuery(id+"F10.wireOp",EDGE,"E15.2.4")])],"isStart":false});
            var Q5;
            Q5=makeQuery(id+"F11.opExtrude","CAP_EDGE",EDGE,{"disambiguationData":[OSD([sQuery(id+"F10.wireOp",EDGE,"E15.1.4")])],"isStart":false});
            chamfer(context, id + "F12", {"entities" : qUnion([Q0, Q1, Q2, Q3, Q4, Q5]), "chamferType" : ChamferType.TWO_OFFSETS, "width1" : 4 * mm, "oppositeDirection" : false, "width2" : 20 * mm, "tangentPropagation" : true});
        }
        {
            var Q0;
            Q0=makeQuery(id+"F3.boolean.opBoolean","COPY",FACE,{"derivedFrom":makeQuery(id+"F3.opExtrude","CAP_FACE",FACE,{"disambiguationData":[OSD([sQuery(id+"F2.wireOp",EDGE,"E7")])],"isStart":false})});
            var sketch = newSketch(context, id + "F13", { "sketchPlane" : qUnion([Q0])});
            skLineSegment(sketch, "E16", {"start": v(0, 0) * mm, "end": v(0, -31.98) * mm, "construction": true});
            skLineSegment(sketch, "E17.bottom", {"start": v(1, -30) * mm, "end": v(-1, -30) * mm});
            skLineSegment(sketch, "E17.top", {"start": v(1, -9) * mm, "end": v(-1, -9) * mm});
            skLineSegment(sketch, "E17.left", {"start": v(1, -30) * mm, "end": v(1, -9) * mm});
            skLineSegment(sketch, "E17.right", {"start": v(-1, -30) * mm, "end": v(-1, -9) * mm});
            skLineSegment(sketch, "E18.1.0", {"start": v(0, 0) * mm, "end": v(27.7, -15.99) * mm, "construction": true});
            skLineSegment(sketch, "E18.1.1", {"start": v(26.48, -14.13) * mm, "end": v(8.3, -3.63) * mm});
            skLineSegment(sketch, "E18.1.2", {"start": v(25.48, -15.87) * mm, "end": v(7.3, -5.37) * mm});
            skLineSegment(sketch, "E18.1.3", {"start": v(26.48, -14.13) * mm, "end": v(25.48, -15.87) * mm});
            skLineSegment(sketch, "E18.1.4", {"start": v(8.3, -3.63) * mm, "end": v(7.3, -5.37) * mm});
            skLineSegment(sketch, "E18.2.0", {"start": v(0, 0) * mm, "end": v(27.7, 15.99) * mm, "construction": true});
            skLineSegment(sketch, "E18.2.1", {"start": v(25.48, 15.87) * mm, "end": v(7.3, 5.37) * mm});
            skLineSegment(sketch, "E18.2.2", {"start": v(26.48, 14.13) * mm, "end": v(8.3, 3.63) * mm});
            skLineSegment(sketch, "E18.2.3", {"start": v(25.48, 15.87) * mm, "end": v(26.48, 14.13) * mm});
            skLineSegment(sketch, "E18.2.4", {"start": v(7.3, 5.37) * mm, "end": v(8.3, 3.63) * mm});
            skLineSegment(sketch, "E18.3.0", {"start": v(0, 0) * mm, "end": v(0, 31.98) * mm, "construction": true});
            skLineSegment(sketch, "E18.3.1", {"start": v(-1, 30) * mm, "end": v(-1, 9) * mm});
            skLineSegment(sketch, "E18.3.2", {"start": v(1, 30) * mm, "end": v(1, 9) * mm});
            skLineSegment(sketch, "E18.3.3", {"start": v(-1, 30) * mm, "end": v(1, 30) * mm});
            skLineSegment(sketch, "E18.3.4", {"start": v(-1, 9) * mm, "end": v(1, 9) * mm});
            skLineSegment(sketch, "E18.4.0", {"start": v(0, 0) * mm, "end": v(-27.7, 15.99) * mm, "construction": true});
            skLineSegment(sketch, "E18.4.1", {"start": v(-26.48, 14.13) * mm, "end": v(-8.3, 3.63) * mm});
            skLineSegment(sketch, "E18.4.2", {"start": v(-25.48, 15.87) * mm, "end": v(-7.3, 5.37) * mm});
            skLineSegment(sketch, "E18.4.3", {"start": v(-26.48, 14.13) * mm, "end": v(-25.48, 15.87) * mm});
            skLineSegment(sketch, "E18.4.4", {"start": v(-8.3, 3.63) * mm, "end": v(-7.3, 5.37) * mm});
            skLineSegment(sketch, "E18.5.0", {"start": v(0, 0) * mm, "end": v(-27.7, -15.99) * mm, "construction": true});
            skLineSegment(sketch, "E18.5.1", {"start": v(-25.48, -15.87) * mm, "end": v(-7.3, -5.37) * mm});
            skLineSegment(sketch, "E18.5.2", {"start": v(-26.48, -14.13) * mm, "end": v(-8.3, -3.63) * mm});
            skLineSegment(sketch, "E18.5.3", {"start": v(-25.48, -15.87) * mm, "end": v(-26.48, -14.13) * mm});
            skLineSegment(sketch, "E18.5.4", {"start": v(-7.3, -5.37) * mm, "end": v(-8.3, -3.63) * mm});
            skPoint(sketch, "E18.center", {"position": v(0, 0) * mm});
            skSolve(sketch);
        }
        {
            var Q0;
            Q0 = qSketchRegion(id + "F13", true);
            extrude(context, id + "F14", {"entities" : qUnion([Q0]), "operationType" : NewBodyOperationType.ADD, "depth" : 4 * mm, "offsetDistance" : 25 * mm});
        }
        {
            var Q0;
            Q0=makeQuery(id+"F14.opExtrude","CAP_EDGE",EDGE,{"disambiguationData":[OSD([sQuery(id+"F13.wireOp",EDGE,"E17.bottom")])],"isStart":false});
            var Q1;
            Q1=makeQuery(id+"F14.opExtrude","CAP_EDGE",EDGE,{"disambiguationData":[OSD([sQuery(id+"F13.wireOp",EDGE,"E18.5.3")])],"isStart":false});
            var Q2;
            Q2=makeQuery(id+"F14.opExtrude","CAP_EDGE",EDGE,{"disambiguationData":[OSD([sQuery(id+"F13.wireOp",EDGE,"E18.4.3")])],"isStart":false});
            var Q3;
            Q3=makeQuery(id+"F14.opExtrude","CAP_EDGE",EDGE,{"disambiguationData":[OSD([sQuery(id+"F13.wireOp",EDGE,"E18.3.3")])],"isStart":false});
            var Q4;
            Q4=makeQuery(id+"F14.opExtrude","CAP_EDGE",EDGE,{"disambiguationData":[OSD([sQuery(id+"F13.wireOp",EDGE,"E18.2.3")])],"isStart":false});
            var Q5;
            Q5=makeQuery(id+"F14.opExtrude","CAP_EDGE",EDGE,{"disambiguationData":[OSD([sQuery(id+"F13.wireOp",EDGE,"E18.1.3")])],"isStart":false});
            chamfer(context, id + "F15", {"entities" : qUnion([Q0, Q1, Q2, Q3, Q4, Q5]), "chamferType" : ChamferType.TWO_OFFSETS, "width1" : 4 * mm, "oppositeDirection" : false, "width2" : 20 * mm, "tangentPropagation" : true});
        }
        {
            var Q0;
            Q0=makeQuery(id+"F3.boolean.opBoolean","COPY",FACE,{"derivedFrom":makeQuery(id+"F3.opExtrude","CAP_FACE",FACE,{"disambiguationData":[OSD([sQuery(id+"F2.wireOp",EDGE,"E7")])],"isStart":false})});
            var Q1;
            Q1=makeQuery(id+"F5.boolean.opBoolean","COPY",FACE,{"derivedFrom":makeQuery(id+"F5.opExtrude","CAP_FACE",FACE,{"disambiguationData":[OSD([sQuery(id+"F4.wireOp",EDGE,"E8")])],"isStart":false})});
            var Q2;
            Q2=makeQuery(id+"F9.opExtrude","SWEPT_FACE",FACE,{"disambiguationData":[OSD([sQuery(id+"F8.wireOp",EDGE,"E11")])]});
            var Q3;
            Q3=makeQuery(id+"F7.opExtrude","SWEPT_FACE",FACE,{"disambiguationData":[OSD([sQuery(id+"F6.wireOp",EDGE,"E9")])]});
            fillet(context, id + "F16", {"entities" : qUnion([Q0, Q1, Q2, Q3]), "radius" : 2 * mm, "tangentPropagation" : true, "allowEdgeOverflow" : false});
        }
        {
            var Q0;
            Q0=makeQuery(id+"F9.opExtrude","CAP_FACE",FACE,{"disambiguationData":[OSD([sQuery(id+"F8.wireOp",EDGE,"E11"),sQuery(id+"F8.wireOp",EDGE,"E12")])],"isStart":false});
            var sketch = newSketch(context, id + "F17", { "sketchPlane" : qUnion([Q0])});
            skLineSegment(sketch, "E19", {"start": v(0, 0) * mm, "end": v(0, 13.9) * mm, "construction": true});
            skLineSegment(sketch, "E20", {"start": v(-8.54, 0) * mm, "end": v(12.05, 0) * mm, "construction": true});
            skLineSegment(sketch, "E21.bottom", {"start": v(-2.25, 8) * mm, "end": v(2.25, 8) * mm});
            skLineSegment(sketch, "E21.top", {"start": v(-2.25, -8) * mm, "end": v(2.25, -8) * mm});
            skLineSegment(sketch, "E21.left", {"start": v(-2.25, 8) * mm, "end": v(-2.25, -8) * mm});
            skLineSegment(sketch, "E21.right", {"start": v(2.25, 8) * mm, "end": v(2.25, -8) * mm});
            skSolve(sketch);
        }
        {
            var Q0;
            Q0 = qSketchRegion(id + "F17", true);
            extrude(context, id + "F18", {"entities" : qUnion([Q0]), "operationType" : NewBodyOperationType.REMOVE, "endBound" : BoundingType.THROUGH_ALL, "oppositeDirection" : true, "depth" : 25 * mm, "offsetDistance" : 25 * mm});
        }
    });
